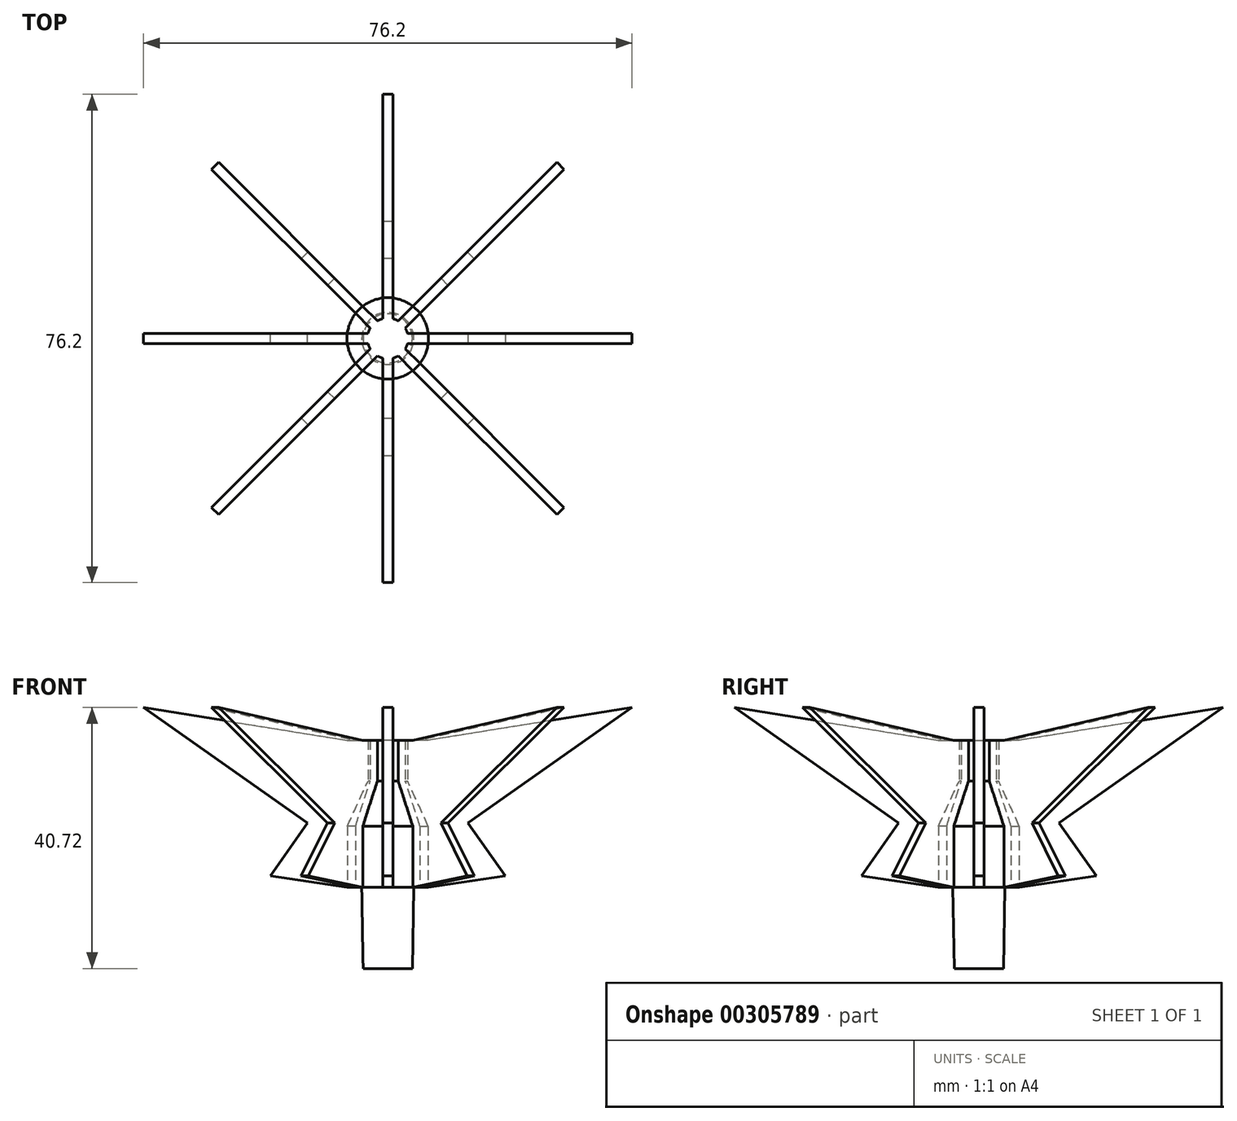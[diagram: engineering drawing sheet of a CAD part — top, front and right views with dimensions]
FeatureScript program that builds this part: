
annotation { "Feature Type Name" : "Feature", "Feature Type Description" : "" }
export const myFeature = defineFeature(function(context is Context, id is Id, definition is map)
    precondition{}
    {
        {
            var Q0;
            Q0=qCreatedBy(makeId("Front.planeOp"),FACE);
            var sketch = newSketch(context, id + "F0", { "sketchPlane" : qUnion([Q0])});
            skLineSegment(sketch, "E0", {"start": v(0, 0) * mm, "end": v(0, 40.21) * mm, "construction": true});
            skLineSegment(sketch, "E1", {"start": v(0, 0) * mm, "end": v(-6.35, 0) * mm});
            skLineSegment(sketch, "E2", {"start": v(-6.35, 0) * mm, "end": v(-6.35, 9.53) * mm});
            skLineSegment(sketch, "E3", {"start": v(-6.35, 9.53) * mm, "end": v(-3.18, 16.56) * mm});
            skLineSegment(sketch, "E4", {"start": v(-3.17, 16.56) * mm, "end": v(-3.17, 22.91) * mm});
            skLineSegment(sketch, "E5", {"start": v(-3.17, 22.91) * mm, "end": v(0, 22.91) * mm});
            skLineSegment(sketch, "E6", {"start": v(0, 22.91) * mm, "end": v(0, 0) * mm});
            skSolve(sketch);
        }
        {
            var Q0;
            Q0=makeQuery(id+"F0.imprint","IMPRINT",FACE,{"disambiguationData":[TD([[makeQuery(id+"F0.imprint","IMPRINT",EDGE,{"derivedFrom":sQuery(id+"F0.wireOp",EDGE,"E1")}),-1.0]])]});
            var Q1;
            Q1=sQuery(id+"F0.wireOp",EDGE,"E0");
            revolve(context, id + "F1", {"entities" : qUnion([Q0]), "axis" : qUnion([Q1]), "revolveType" : RevolveType.FULL});
        }
        {
            var Q0;
            Q0=makeQuery(id+"F1.opRevolve","SWEPT_FACE",FACE,{"disambiguationData":[OSD([sQuery(id+"F0.wireOp",EDGE,"E1")])]});
            var sketch = newSketch(context, id + "F2", { "sketchPlane" : qUnion([Q0])});
            skCircle(sketch, "E7", {"center": v(0, 0) * mm, "radius": 4.06 * mm});
            skSolve(sketch);
        }
        {
            var Q0;
            Q0 = qSketchRegion(id + "F2", true);
            extrude(context, id + "F3", {"entities" : qUnion([Q0]), "operationType" : NewBodyOperationType.ADD, "depth" : 12.7 * mm, "hasDraft" : true, "draftAngle" : 1 * degree, "draftPullDirection" : true});
        }
        {
            var Q0;
            Q0=qCreatedBy(makeId("Front.planeOp"),FACE);
            var sketch = newSketch(context, id + "F4", { "sketchPlane" : qUnion([Q0])});
            skLineSegment(sketch, "E8", {"start": v(-3.17, 16.56) * mm, "end": v(-3.17, 22.91) * mm, "construction": true});
            skLineSegment(sketch, "E9", {"start": v(-6.38, 9.46) * mm, "end": v(-3.18, 16.56) * mm, "construction": true});
            skLineSegment(sketch, "E10", {"start": v(-6.35, 0) * mm, "end": v(-6.35, 9.53) * mm, "construction": true});
            skLineSegment(sketch, "E11.0", {"start": v(3.17, 22.91) * mm, "end": v(-3.17, 22.91) * mm, "construction": true});
            skLineSegment(sketch, "E12", {"start": v(-6.35, 0) * mm, "end": v(-18.32, 1.75) * mm});
            skLineSegment(sketch, "E13", {"start": v(-18.32, 1.75) * mm, "end": v(-12.5, 10) * mm});
            skLineSegment(sketch, "E14", {"start": v(-12.5, 10) * mm, "end": v(-38.1, 28.02) * mm});
            skLineSegment(sketch, "E15", {"start": v(-38.1, 28.02) * mm, "end": v(-6.35, 22.91) * mm});
            skLineSegment(sketch, "E16", {"start": v(-6.35, 22.91) * mm, "end": v(-3.17, 22.91) * mm});
            skLineSegment(sketch, "E17", {"start": v(-3.17, 22.91) * mm, "end": v(-2.86, 22.91) * mm});
            skLineSegment(sketch, "E18", {"start": v(-2.86, 22.91) * mm, "end": v(-2.86, 16.5) * mm});
            skLineSegment(sketch, "E19", {"start": v(-2.86, 16.5) * mm, "end": v(-6.03, 9.46) * mm});
            skLineSegment(sketch, "E20", {"start": v(-6.03, 9.46) * mm, "end": v(-6.03, 0) * mm});
            skLineSegment(sketch, "E21", {"start": v(-6.03, 0) * mm, "end": v(-6.35, 0) * mm});
            skSolve(sketch);
        }
        {
            var Q0;
            Q0=makeQuery(id+"F4.imprint","IMPRINT",FACE,{"disambiguationData":[TD([[makeQuery(id+"F4.imprint","IMPRINT",EDGE,{"derivedFrom":sQuery(id+"F4.wireOp",EDGE,"E12")}),-1.0]])]});
            extrude(context, id + "F5", {"entities" : qUnion([Q0]), "depth" : 1.59 * mm, "symmetric" : true});
        }
        {
            var Q0;
            Q0=makeQuery(id+"F5.opExtrude","SWEPT_BODY",BODY,{"disambiguationData":[OSD([sQuery(id+"F4.wireOp",EDGE,"E12"),sQuery(id+"F4.wireOp",EDGE,"E13"),sQuery(id+"F4.wireOp",EDGE,"E14"),sQuery(id+"F4.wireOp",EDGE,"E15"),sQuery(id+"F4.wireOp",EDGE,"E16"),sQuery(id+"F4.wireOp",EDGE,"E17"),sQuery(id+"F4.wireOp",EDGE,"E18"),sQuery(id+"F4.wireOp",EDGE,"E19"),sQuery(id+"F4.wireOp",EDGE,"E20"),sQuery(id+"F4.wireOp",EDGE,"E21")])]});
            var Q1;
            Q1=sQuery(id+"F0.wireOp",EDGE,"E0");
            circularPattern(context, id + "F6", {"operationType" : NewBodyOperationType.ADD, "entities" : qUnion([Q0]), "axis" : qUnion([Q1]), "angle" : 360 * degree, "instanceCount" : 8, "equalSpace" : true});
        }
    });
